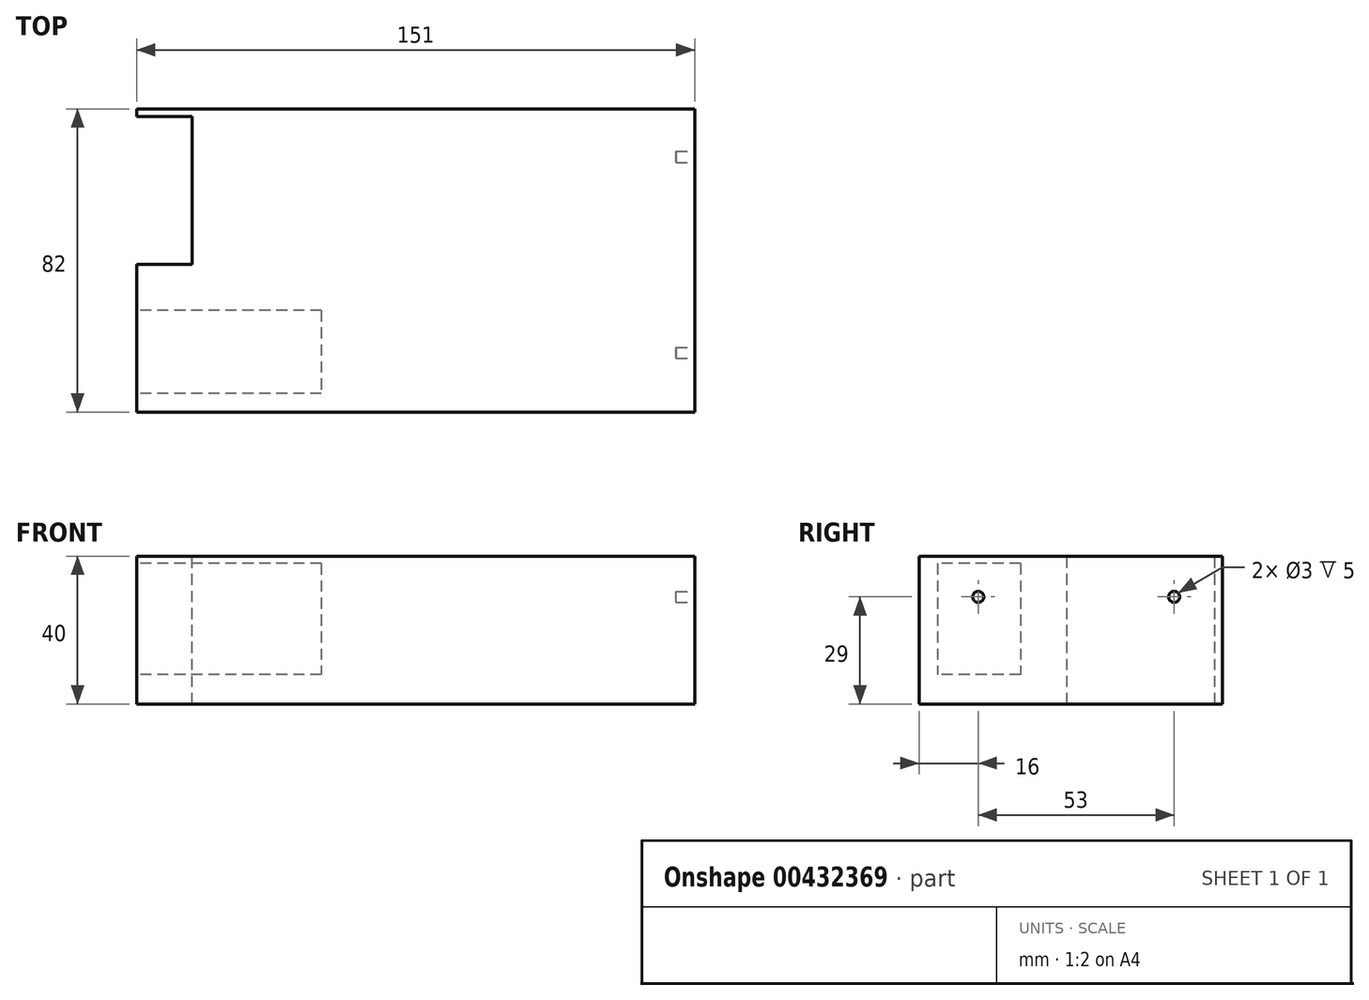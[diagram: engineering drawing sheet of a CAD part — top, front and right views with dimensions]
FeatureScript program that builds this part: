
annotation { "Feature Type Name" : "Feature", "Feature Type Description" : "" }
export const myFeature = defineFeature(function(context is Context, id is Id, definition is map)
    precondition{}
    {
        {
            var Q0;
            Q0=qCreatedBy(makeId("Top.planeOp"),FACE);
            var sketch = newSketch(context, id + "F0", { "sketchPlane" : qUnion([Q0])});
            skLineSegment(sketch, "E0.bottom", {"start": v(-75.5, 41) * mm, "end": v(75.5, 41) * mm});
            skLineSegment(sketch, "E0.top", {"start": v(-75.5, -41) * mm, "end": v(75.5, -41) * mm});
            skLineSegment(sketch, "E0.left", {"start": v(-75.5, 41) * mm, "end": v(-75.5, -41) * mm});
            skLineSegment(sketch, "E0.right", {"start": v(75.5, 41) * mm, "end": v(75.5, -41) * mm});
            skSolve(sketch);
        }
        {
            var Q0;
            Q0 = qSketchRegion(id + "F0", true);
            extrude(context, id + "F1", {"entities" : qUnion([Q0]), "depth" : 40 * mm});
        }
        {
            var Q0;
            Q0=makeQuery(id+"F1.opExtrude","CAP_FACE",FACE,{"disambiguationData":[OSD([sQuery(id+"F0.wireOp",EDGE,"E0.bottom"),sQuery(id+"F0.wireOp",EDGE,"E0.top"),sQuery(id+"F0.wireOp",EDGE,"E0.left"),sQuery(id+"F0.wireOp",EDGE,"E0.right")])],"isStart":false});
            var sketch = newSketch(context, id + "F2", { "sketchPlane" : qUnion([Q0])});
            skLineSegment(sketch, "E1.bottom", {"start": v(-60.5, 39) * mm, "end": v(-75.5, 39) * mm});
            skLineSegment(sketch, "E1.top", {"start": v(-60.5, -1) * mm, "end": v(-75.5, -1) * mm});
            skLineSegment(sketch, "E1.left", {"start": v(-60.5, 39) * mm, "end": v(-60.5, -1) * mm});
            skLineSegment(sketch, "E1.right", {"start": v(-75.5, 39) * mm, "end": v(-75.5, -1) * mm});
            skSolve(sketch);
        }
        {
            var Q0;
            Q0 = qSketchRegion(id + "F2", true);
            extrude(context, id + "F3", {"entities" : qUnion([Q0]), "operationType" : NewBodyOperationType.REMOVE, "oppositeDirection" : true, "depth" : 41 * mm});
        }
        {
            var Q0;
            {var subQ1=sQuery(id+"F0.wireOp",EDGE,"E0.left");var subQ2=sQuery(id+"F0.wireOp",EDGE,"E0.top");Q0=makeQuery(id+"F3.boolean.opBoolean","SPLIT",FACE,{"disambiguationData":[TD([makeQuery(id+"F1.opExtrude","SWEPT_FACE",FACE,{"disambiguationData":[OSD([subQ2])]})])],"derivedFrom":makeQuery(id+"F1.opExtrude","SWEPT_FACE",FACE,{"disambiguationData":[OSD([subQ1])]})});}
            var sketch = newSketch(context, id + "F4", { "sketchPlane" : qUnion([Q0])});
            skLineSegment(sketch, "E2.bottom", {"start": v(13.5, 38) * mm, "end": v(36, 38) * mm});
            skLineSegment(sketch, "E2.top", {"start": v(13.5, 8) * mm, "end": v(36, 8) * mm});
            skLineSegment(sketch, "E2.left", {"start": v(13.5, 38) * mm, "end": v(13.5, 8) * mm});
            skLineSegment(sketch, "E2.right", {"start": v(36, 38) * mm, "end": v(36, 8) * mm});
            skSolve(sketch);
        }
        {
            var Q0;
            Q0 = qSketchRegion(id + "F4", true);
            extrude(context, id + "F5", {"entities" : qUnion([Q0]), "operationType" : NewBodyOperationType.REMOVE, "oppositeDirection" : true, "depth" : 50 * mm});
        }
        {
            var Q0;
            Q0=makeQuery(id+"F1.opExtrude","SWEPT_FACE",FACE,{"disambiguationData":[OSD([sQuery(id+"F0.wireOp",EDGE,"E0.right")])]});
            var sketch = newSketch(context, id + "F6", { "sketchPlane" : qUnion([Q0])});
            skCircle(sketch, "E3", {"center": v(-25, 29) * mm, "radius": 1.5 * mm});
            skPoint(sketch, "E4.start.orphan", {"position": v(0, 40) * mm});
            skCircle(sketch, "E5", {"center": v(28, 29) * mm, "radius": 1.5 * mm});
            skSolve(sketch);
        }
        {
            var Q0;
            Q0 = qSketchRegion(id + "F6", true);
            extrude(context, id + "F7", {"entities" : qUnion([Q0]), "operationType" : NewBodyOperationType.REMOVE, "oppositeDirection" : true, "depth" : 5 * mm});
        }
    });
